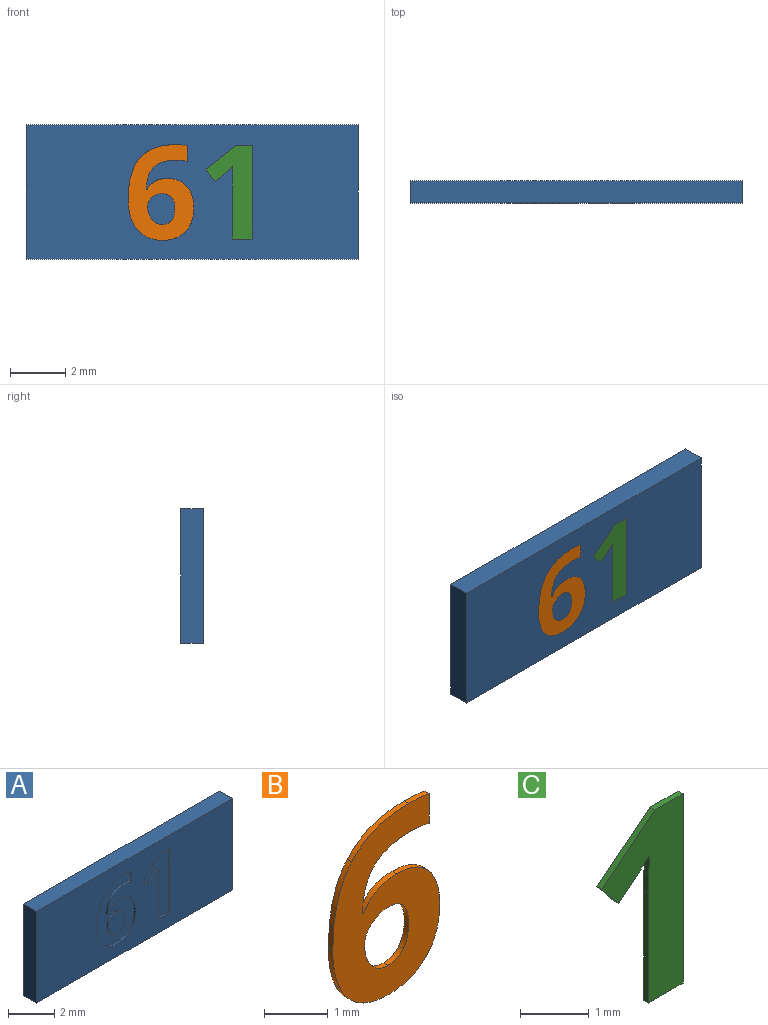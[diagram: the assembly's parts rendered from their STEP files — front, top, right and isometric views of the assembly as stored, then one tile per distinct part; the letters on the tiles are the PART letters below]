
ASSEMBLY  parts=3 mates=2
PART A: 44 faces, bbox 12x0.8x4.9 mm
  f0: plane 12x4.85mm, normal (0,-1,0), area 49.5mm2, adj f1,f2,f3,f4,f6,f7,f8,f9
  f1: plane 12x0.8mm, normal (0,0,-1), area 9.6mm2, adj f0,f2,f4,f5
  f2: plane 4.85x0.8mm, normal (1,0,0), area 3.9mm2, adj f0,f1,f3,f5
  f3: plane 12x0.8mm, normal (0,0,1), area 9.6mm2, adj f0,f2,f4,f5
  f4: plane 4.85x0.8mm, normal (-1,0,0), area 3.9mm2, adj f0,f1,f3,f5
  f5: plane 12x4.85mm, normal (0,1,0), area 58.2mm2, adj f1,f2,f3,f4
  f6: extruded ~0.8x0.15mm, area 0.1mm2, adj f0,f7,f30,f31
  f7: extruded ~0.51x0.43mm, area 0.1mm2, adj f0,f6,f8,f31
  f8: extruded ~0.65x0.17mm, area 0.1mm2, adj f0,f7,f9,f31
  f9: extruded ~0.84x0.32mm, area 0.1mm2, adj f0,f8,f10,f31
  f10: extruded ~0.85x0.3mm, area 0.1mm2, adj f0,f9,f11,f31
  f11: extruded ~0.78x0.26mm, area 0.1mm2, adj f0,f10,f12,f31
  f12: extruded ~0.71x0.28mm, area 0.1mm2, adj f0,f11,f13,f31
  f13: extruded ~0.73x0.39mm, area 0.1mm2, adj f0,f12,f14,f31
  f14: plane 0.1x0.03mm, normal (0,0,-1), area 0mm2, adj f0,f13,f15,f31
  f15: extruded ~0.62x0.14mm, area 0.1mm2, adj f0,f14,f16,f31
  f16: extruded ~0.35x0.33mm, area 0mm2, adj f0,f15,f17,f31
  f17: extruded ~0.6x0.11mm, area 0.1mm2, adj f0,f16,f18,f31
  f18: extruded ~0.41x0.1mm, area 0mm2, adj f0,f17,f19,f31
  f19: plane 0.57x0.1mm, normal (-1,0,0), area 0.1mm2, adj f0,f18,f20,f31
  f20: extruded ~0.45x0.1mm, area 0mm2, adj f0,f19,f21,f31
  f21: extruded ~1.27x0.49mm, area 0.1mm2, adj f0,f20,f30,f31
  f22: extruded ~0.37x0.19mm, area 0mm2, adj f23,f29,f31,f32
  f23: extruded ~0.46x0.14mm, area 0mm2, adj f22,f24,f31,f32
  f24: extruded ~0.33x0.15mm, area 0mm2, adj f23,f25,f31,f32
  f25: extruded ~0.37x0.14mm, area 0mm2, adj f24,f26,f31,f32
  f26: extruded ~0.34x0.14mm, area 0mm2, adj f25,f27,f31,f32
  f27: extruded ~0.39x0.11mm, area 0mm2, adj f26,f28,f31,f32
  f28: extruded ~0.44x0.12mm, area 0mm2, adj f27,f29,f31,f32
  f29: extruded ~0.35x0.15mm, area 0mm2, adj f22,f28,f31,f32
  f30: extruded ~1.49x0.42mm, area 0.2mm2, adj f0,f6,f21,f31
  f31: plane 3.46x2.38mm, normal (0,-1,0), area 4.8mm2, adj f6,f7,f8,f9,f10,f11,f12,f13
  f32: plane 1.12x0.98mm, normal (0,-1,0), area 0.9mm2, adj f22,f23,f24,f25,f26,f27,f28,f29
  f33: plane 3.37x0.1mm, normal (-1,0,0), area 0.3mm2, adj f0,f34,f42,f43
  f34: plane 0.59x0.1mm, normal (0,0,-1), area 0.1mm2, adj f0,f33,f35,f43
  f35: plane 1.09x0.86mm, normal (0.62,0,-0.78), area 0.1mm2, adj f0,f34,f36,f43
  f36: plane 0.43x0.34mm, normal (0.78,0,0.63), area 0.1mm2, adj f0,f35,f37,f43
  f37: plane 0.39x0.31mm, normal (-0.63,0,0.78), area 0mm2, adj f0,f36,f38,f43
  f38: extruded ~0.25x0.23mm, area 0mm2, adj f0,f37,f39,f43
  f39: plane 0.35x0.1mm, normal (1,0,-0.03), area 0mm2, adj f0,f38,f40,f43
  f40: plane 0.32x0.1mm, normal (1,0,-0.02), area 0mm2, adj f0,f39,f41,f43
  f41: plane 1.95x0.1mm, normal (1,0,0), area 0.2mm2, adj f0,f40,f42,f43
  f42: plane 0.71x0.1mm, normal (0,0,1), area 0.1mm2, adj f0,f33,f41,f43
  f43: plane 3.37x1.67mm, normal (0,-1,0), area 2.9mm2, adj f33,f34,f35,f36,f37,f38,f39,f40
PART B: 27 faces, bbox 2.4x0.1x3.5 mm
  f0: plane 3.46x2.38mm, normal (0,-1,0), area 4.8mm2, adj f1,f2,f3,f4,f5,f6,f7,f8
  f1: extruded ~0.51x0.43mm, area 0.1mm2, adj f0,f2,f20,f22
  f2: extruded ~0.65x0.17mm, area 0.1mm2, adj f0,f1,f3,f20
  f3: extruded ~0.84x0.32mm, area 0.1mm2, adj f0,f2,f4,f20
  f4: extruded ~0.85x0.3mm, area 0.1mm2, adj f0,f3,f5,f20
  f5: extruded ~0.78x0.26mm, area 0.1mm2, adj f0,f4,f6,f20
  f6: extruded ~0.71x0.28mm, area 0.1mm2, adj f0,f5,f7,f20
  f7: extruded ~0.73x0.39mm, area 0.1mm2, adj f0,f6,f8,f20
  f8: plane 0.1x0.03mm, normal (0,0,1), area 0mm2, adj f0,f7,f9,f20
  f9: extruded ~0.62x0.14mm, area 0.1mm2, adj f0,f8,f10,f20
  f10: extruded ~0.35x0.33mm, area 0mm2, adj f0,f9,f11,f20
  f11: extruded ~0.6x0.11mm, area 0.1mm2, adj f0,f10,f12,f20
  f12: extruded ~0.41x0.1mm, area 0mm2, adj f0,f11,f13,f20
  f13: plane 0.57x0.1mm, normal (1,0,0), area 0.1mm2, adj f0,f12,f14,f20
  f14: extruded ~0.45x0.1mm, area 0mm2, adj f0,f13,f20,f21
  f15: extruded ~0.46x0.14mm, area 0mm2, adj f0,f16,f20,f25
  f16: extruded ~0.33x0.15mm, area 0mm2, adj f0,f15,f17,f20
  f17: extruded ~0.37x0.14mm, area 0mm2, adj f0,f16,f18,f20
  f18: extruded ~0.34x0.14mm, area 0mm2, adj f0,f17,f19,f20
  f19: extruded ~0.39x0.11mm, area 0mm2, adj f0,f18,f20,f24
  f20: plane 3.46x2.38mm, normal (0,1,0), area 4.8mm2, adj f1,f2,f3,f4,f5,f6,f7,f8
  f21: extruded ~1.27x0.49mm, area 0.1mm2, adj f0,f14,f20,f23
  f22: extruded ~0.8x0.15mm, area 0.1mm2, adj f0,f1,f20,f23
  f23: extruded ~1.49x0.42mm, area 0.2mm2, adj f0,f20,f21,f22
  f24: extruded ~0.44x0.12mm, area 0mm2, adj f0,f19,f20,f26
  f25: extruded ~0.37x0.19mm, area 0mm2, adj f0,f15,f20,f26
  f26: extruded ~0.35x0.15mm, area 0mm2, adj f0,f20,f24,f25
PART C: 12 faces, bbox 1.7x0.1x3.4 mm
  f0: plane 3.37x1.67mm, normal (0,-1,0), area 2.9mm2, adj f1,f2,f3,f4,f5,f6,f7,f9
  f1: plane 0.59x0.1mm, normal (0,0,1), area 0.1mm2, adj f0,f2,f8,f10
  f2: plane 1.09x0.86mm, normal (-0.62,0,0.78), area 0.1mm2, adj f0,f1,f3,f8
  f3: plane 0.43x0.34mm, normal (-0.78,0,-0.63), area 0.1mm2, adj f0,f2,f4,f8
  f4: plane 0.39x0.31mm, normal (0.63,0,-0.78), area 0mm2, adj f0,f3,f5,f8
  f5: extruded ~0.25x0.23mm, area 0mm2, adj f0,f4,f6,f8
  f6: plane 0.35x0.1mm, normal (-1,0,0.03), area 0mm2, adj f0,f5,f7,f8
  f7: plane 0.32x0.1mm, normal (-1,0,0.02), area 0mm2, adj f0,f6,f8,f9
  f8: plane 3.37x1.67mm, normal (0,1,0), area 2.9mm2, adj f1,f2,f3,f4,f5,f6,f7,f9
  f9: plane 1.95x0.1mm, normal (-1,0,0), area 0.2mm2, adj f0,f7,f8,f11
  f10: plane 3.37x0.1mm, normal (1,0,0), area 0.3mm2, adj f0,f1,f8,f11
  f11: plane 0.71x0.1mm, normal (0,0,-1), area 0.1mm2, adj f0,f8,f9,f10
PLACE A t=(-0.03,0.38,-0.01)mm
PLACE B t=(-2.65,0.38,-0.01)mm
PLACE C t=(-0.25,0.38,-0.01)mm
MATE fastened C.f0 <-> A.f0  axis (0,-1,0) through (1.43,-0.42,-1.71)mm
MATE fastened B.f0 <-> A.f0  axis (0,-1,0) through (-0.2,-0.42,1.09)mm
